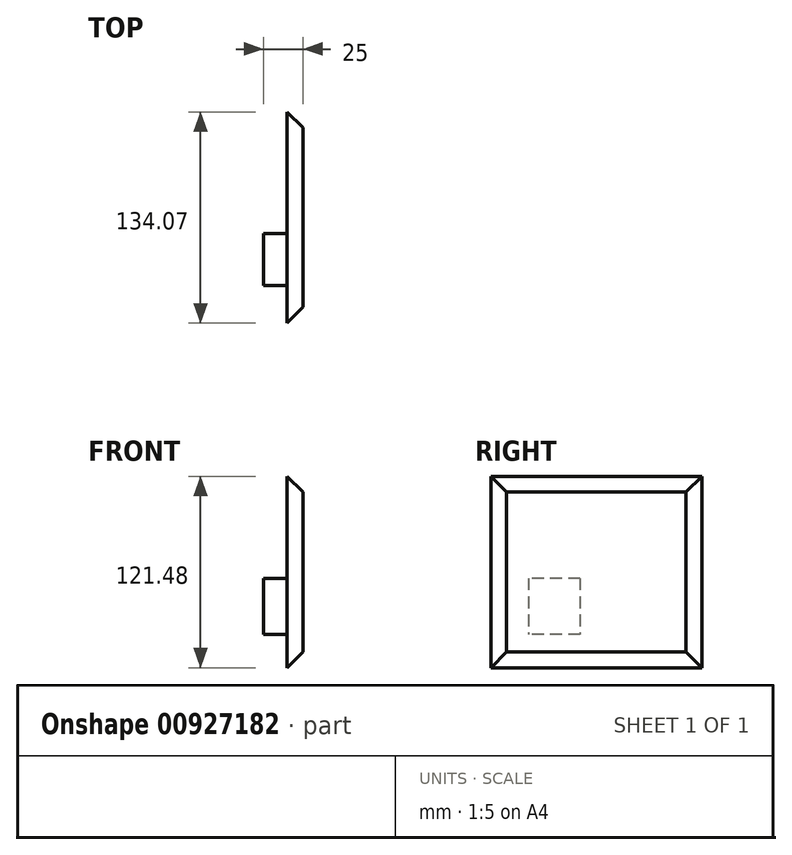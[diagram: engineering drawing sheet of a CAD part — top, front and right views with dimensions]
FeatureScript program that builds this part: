
annotation { "Feature Type Name" : "Feature", "Feature Type Description" : "" }
export const myFeature = defineFeature(function(context is Context, id is Id, definition is map)
    precondition{}
    {
        {
            var Q0;
            Q0=qCreatedBy(makeId("Right.planeOp"),FACE);
            var sketch = newSketch(context, id + "F0", { "sketchPlane" : qUnion([Q0])});
            skPoint(sketch, "E0.0", {"position": v(-54.37, 0) * mm});
            skPoint(sketch, "E0.1", {"position": v(60.22, 0) * mm});
            skLineSegment(sketch, "E1.bottom", {"start": v(-33.2, -49.27) * mm, "end": v(80.88, -49.27) * mm});
            skLineSegment(sketch, "E1.top", {"start": v(-33.2, 52.21) * mm, "end": v(80.88, 52.21) * mm});
            skLineSegment(sketch, "E1.left", {"start": v(-33.2, -49.27) * mm, "end": v(-33.2, 52.21) * mm});
            skLineSegment(sketch, "E1.right", {"start": v(80.88, -49.27) * mm, "end": v(80.88, 52.21) * mm});
            skSolve(sketch);
        }
        {
            var Q0;
            Q0=makeQuery(id+"F0.imprint","IMPRINT",FACE,{"disambiguationData":[TD([[makeQuery(id+"F0.imprint","IMPRINT",EDGE,{"derivedFrom":sQuery(id+"F0.wireOp",EDGE,"E1.bottom")}),1.0]])]});
            extrude(context, id + "F1", {"entities" : qUnion([Q0]), "oppositeDirection" : true, "depth" : 10 * mm, "offsetDistance" : 25 * mm, "hasDraft" : true, "draftAngle" : 45 * degree});
        }
        {
            var Q0;
            Q0=makeQuery(id+"F1.opExtrude","CAP_FACE",FACE,{"disambiguationData":[OSD([sQuery(id+"F0.wireOp",EDGE,"E1.bottom"),sQuery(id+"F0.wireOp",EDGE,"E1.top"),sQuery(id+"F0.wireOp",EDGE,"E1.left"),sQuery(id+"F0.wireOp",EDGE,"E1.right")])],"isStart":true});
            var sketch = newSketch(context, id + "F2", { "sketchPlane" : qUnion([Q0])});
            skLineSegment(sketch, "E2.bottom", {"start": v(13.54, -2.5) * mm, "end": v(-19.34, -2.5) * mm});
            skLineSegment(sketch, "E2.top", {"start": v(13.54, -38) * mm, "end": v(-19.34, -38) * mm});
            skLineSegment(sketch, "E2.left", {"start": v(13.54, -2.5) * mm, "end": v(13.54, -38) * mm});
            skLineSegment(sketch, "E2.right", {"start": v(-19.34, -2.5) * mm, "end": v(-19.34, -38) * mm});
            skSolve(sketch);
        }
        {
            var Q0;
            Q0 = qSketchRegion(id + "F2", true);
            extrude(context, id + "F3", {"entities" : qUnion([Q0]), "operationType" : NewBodyOperationType.ADD, "oppositeDirection" : true, "depth" : 25 * mm, "offsetDistance" : 25 * mm});
        }
    });
